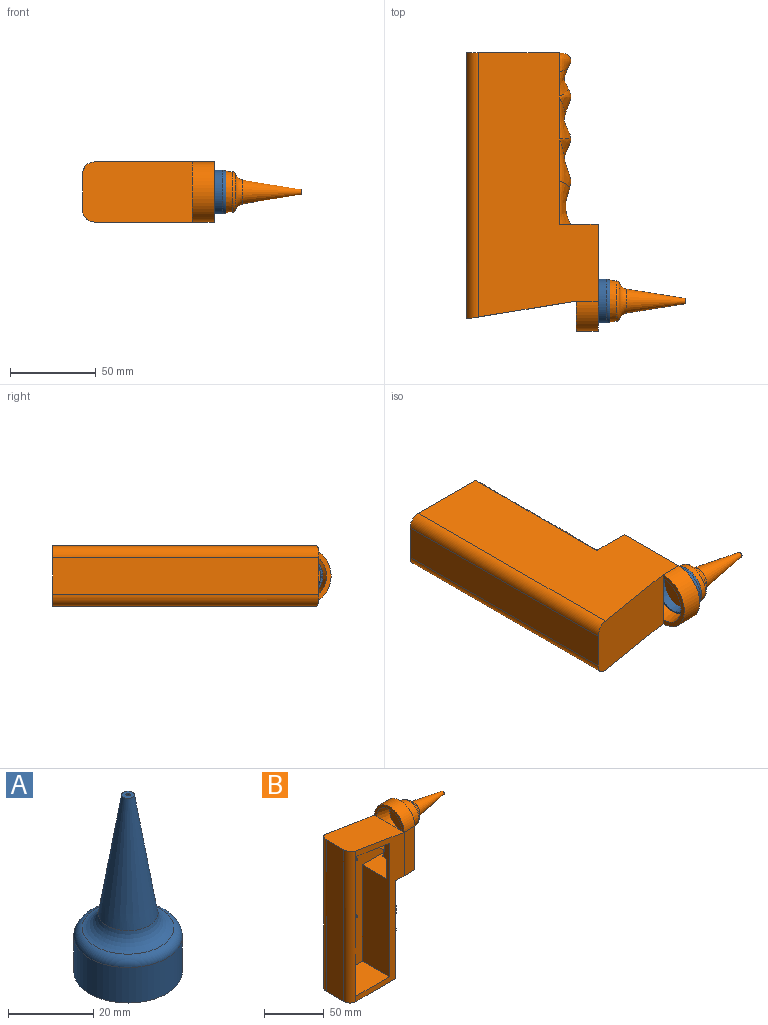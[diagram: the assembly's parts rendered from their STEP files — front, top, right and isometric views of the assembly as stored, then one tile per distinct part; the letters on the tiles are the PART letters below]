
ASSEMBLY  parts=2 mates=1
PART A: 10 faces, bbox 27.5x27.5x50.8 mm
  f0: cylinder r=12.7mm len=25.4mm, axis (0,0,-1), area 810.7mm2, adj f1,f4
  f1: plane 25.4x25.4mm, normal (0,0,-1), area 76.9mm2, adj f0,f9
  f2: plane 3x3mm, normal (0,0,1), area 6.3mm2, adj f3,f6
  f3: cone r=7.62mm half-angle=9.1deg, axis (0,0,-1), area 919.8mm2, adj f2,f5
  f4: torus R=10.16mm, axis (0,0,1), area 256.1mm2, adj f0,f5
  f5: torus R=11.91mm, axis (0,0,1), area 312.6mm2, adj f3,f4
  f6: cone r=0.49mm half-angle=7.5deg, axis (0,0,-1), area 589.5mm2, adj f2,f7
  f7: torus R=10.92mm, axis (0,0,1), area 310.4mm2, adj f6,f8
  f8: torus R=9.26mm, axis (0,0,1), area 126.3mm2, adj f7,f9
  f9: cone r=10.8mm half-angle=5deg, axis (0,0,-1), area 730.2mm2, adj f1,f8
PART B: 65 faces, bbox 128x35.7x162.6 mm
  f0: plane 25.32x0.5mm, normal (1,0,0), area 1mm2, adj f13,f52
  f1: plane 17.62x12.64mm, normal (1,0,0), area 9.6mm2, adj f12,f13,f46
  f2: plane 25.32x0.5mm, normal (1,0,0), area 1mm2, adj f6,f45
  f3: plane 29.53x3mm, normal (1,0,0), area 88mm2, adj f10,f24,f30
  f4: plane 17.96x9.11mm, normal (-1,0,0), area 117.5mm2, adj f21,f23,f26,f29
  f5: plane 35x17.5mm, normal (-1,0,0), area 138.6mm2, adj f10,f16,f24
  f6: plane 153.89x69.7mm, normal (0,-1,0), area 1948.9mm2, adj f2,f7,f8,f9,f10,f12,f15,f16
  f7: plane 17.62x12.64mm, normal (1,0,0), area 9.6mm2, adj f6,f12,f39
  f8: plane 35x22.7mm, normal (0,0,-1), area 630.7mm2, adj f6,f9,f13,f17,f18,f45,f52
  f9: plane 44.6x0mm, normal (1,0,0), area 0mm2, adj f6,f8,f17
  f10: plane 64.45x35.48mm, normal (0.16,0,0.99), area 2247mm2, adj f3,f5,f6,f11,f13,f14,f15
  f11: plane 155x21mm, normal (-1,0,0), area 3255mm2, adj f10,f12,f14,f15
  f12: plane 53.97x35mm, normal (0,0,-1), area 1867.9mm2, adj f1,f6,f7,f11,f13,f14,f15
  f13: plane 153.89x69.7mm, normal (0,1,0), area 8068.1mm2, adj f0,f1,f8,f10,f12,f14,f16,f18
  f14: cylinder r=7mm len=155mm, axis (0,0,-1), area 1698.1mm2, adj f10,f11,f12,f13
  f15: cylinder r=7mm len=155mm, axis (0,0,1), area 1698.1mm2, adj f6,f10,f11,f12,f22
  f16: cylinder r=17.5mm len=35mm, axis (-1,0,0), area 698.2mm2, adj f5,f6,f13,f18
  f17: plane 44.6x12.7mm, normal (0,-1,0), area 566.4mm2, adj f6,f8,f9,f18
  f18: plane 62.1x35mm, normal (1,0,0), area 1535.3mm2, adj f6,f8,f13,f16,f17,f54
  f19: plane 39.79x32mm, normal (0,0,1), area 1273.3mm2, adj f6,f20,f22,f23
  f20: plane 136.82x32.5mm, normal (-1,0,0), area 3330.5mm2, adj f6,f19,f21,f23,f25,f26,f27,f29
  f21: plane 39.79x32mm, normal (-0.16,0,-0.99), area 1290mm2, adj f4,f6,f20,f22,f23,f30
  f22: plane 142.79x32mm, normal (1,0,0), area 4569.3mm2, adj f15,f19,f21,f23
  f23: plane 142.79x64.79mm, normal (0,-1,0), area 6042.1mm2, adj f4,f19,f20,f21,f22,f26,f27,f28
  f24: cone r=12.06mm half-angle=12deg, axis (-1,0,0), area 1094.4mm2, adj f3,f5,f29,f53
  f25: plane 25x20.36mm, normal (0,1,0), area 509mm2, adj f20,f26,f27,f28
  f26: plane 29x25mm, normal (0,0,-1), area 640.9mm2, adj f4,f20,f23,f25,f28,f29
  f27: plane 29x25mm, normal (0,0,1), area 725mm2, adj f20,f23,f25,f28
  f28: plane 29x20.36mm, normal (-1,0,0), area 590.4mm2, adj f23,f25,f26,f27
  f29: bspline ~28.91x21mm, area 729.9mm2, adj f4,f20,f24,f26,f30
  f30: bspline ~28.91x17.18mm, area 411.6mm2, adj f3,f21,f29
  f31: cone r=1.25mm half-angle=2deg, axis (0,1,0), area 36.5mm2, adj f23,f32
  f32: plane 2.15x2.15mm, normal (0,-1,0), area 3.6mm2, adj f31
  f33: cone r=1.25mm half-angle=2deg, axis (0,1,0), area 36.5mm2, adj f23,f34
  f34: plane 2.15x2.15mm, normal (0,-1,0), area 3.6mm2, adj f33
  f35: cone r=1.25mm half-angle=2deg, axis (0,1,0), area 36.5mm2, adj f23,f36
  f36: plane 2.15x2.15mm, normal (0,-1,0), area 3.6mm2, adj f35
  f37: cone r=1.25mm half-angle=2deg, axis (0,1,0), area 36.5mm2, adj f23,f38
  f38: plane 2.15x2.15mm, normal (0,-1,0), area 3.6mm2, adj f37
  f39: bspline ~17.5x10.81mm, area 225.5mm2, adj f7,f40,f46
  f40: bspline ~17.5x16.35mm, area 253mm2, adj f6,f39,f41,f47
  f41: bspline ~17.5x14.51mm, area 186.8mm2, adj f6,f40,f42,f48
  f42: bspline ~22.82x17.5mm, area 330.8mm2, adj f6,f41,f43,f49
  f43: bspline ~17.5x13.8mm, area 168mm2, adj f6,f42,f44,f50
  f44: bspline ~27.27x17.5mm, area 357.8mm2, adj f6,f43,f45,f51
  f45: bspline ~25x17.5mm, area 436.2mm2, adj f2,f8,f44,f52
  f46: bspline ~17.5x10.81mm, area 225.5mm2, adj f1,f39,f47
  f47: bspline ~17.5x16.35mm, area 253mm2, adj f13,f40,f46,f48
  f48: bspline ~17.5x14.51mm, area 186.8mm2, adj f13,f41,f47,f49
  f49: bspline ~22.82x17.5mm, area 330.8mm2, adj f13,f42,f48,f50
  f50: bspline ~17.5x13.8mm, area 168mm2, adj f13,f43,f49,f51
  f51: bspline ~27.27x17.5mm, area 357.8mm2, adj f13,f44,f50,f52
  f52: bspline ~25x17.5mm, area 436.2mm2, adj f0,f8,f45,f51
  f53: plane 24.13x24.13mm, normal (-1,0,0), area 457.3mm2, adj f24
  f54: cone r=12.7mm half-angle=5deg, axis (-1,0,0), area 801.8mm2, adj f18,f57
  f55: plane 3x3mm, normal (1,0,0), area 7.1mm2, adj f56
  f56: cone r=7.62mm half-angle=9.1deg, axis (-1,0,0), area 932.9mm2, adj f55,f58
  f57: torus R=9.26mm, axis (1,0,0), area 199.5mm2, adj f54,f58
  f58: torus R=11.96mm, axis (1,0,0), area 271.1mm2, adj f56,f57
  f59: cone r=11.73mm half-angle=89.9deg, axis (1,0,0), area 432.4mm2, adj f60
  f60: cone r=10.9mm half-angle=5.1deg, axis (-1,0,0), area 663.2mm2, adj f59,f61
  f61: torus R=9.36mm, axis (-1,0,0), area 113.8mm2, adj f60,f62
  f62: torus R=12.04mm, axis (-1,0,0), area 299.7mm2, adj f61,f63
  f63: cone r=0.65mm half-angle=9.3deg, axis (-1,0,0), area 722.8mm2, adj f62,f64
  f64: cone r=0mm half-angle=89.9deg, axis (1,0,0), area 1.3mm2, adj f63
PLACE A rot(axis=(0.58,0.58,0.58),120deg) t=(-14.68,1.5,-24.05)mm
PLACE B rot(axis=(1,0,0),90deg) t=(-86.27,46.1,-6.55)mm
MATE slider B.f16 <-> A.f0  axis (-1,0,0) through (-9.6,1.5,-24.05)mm
